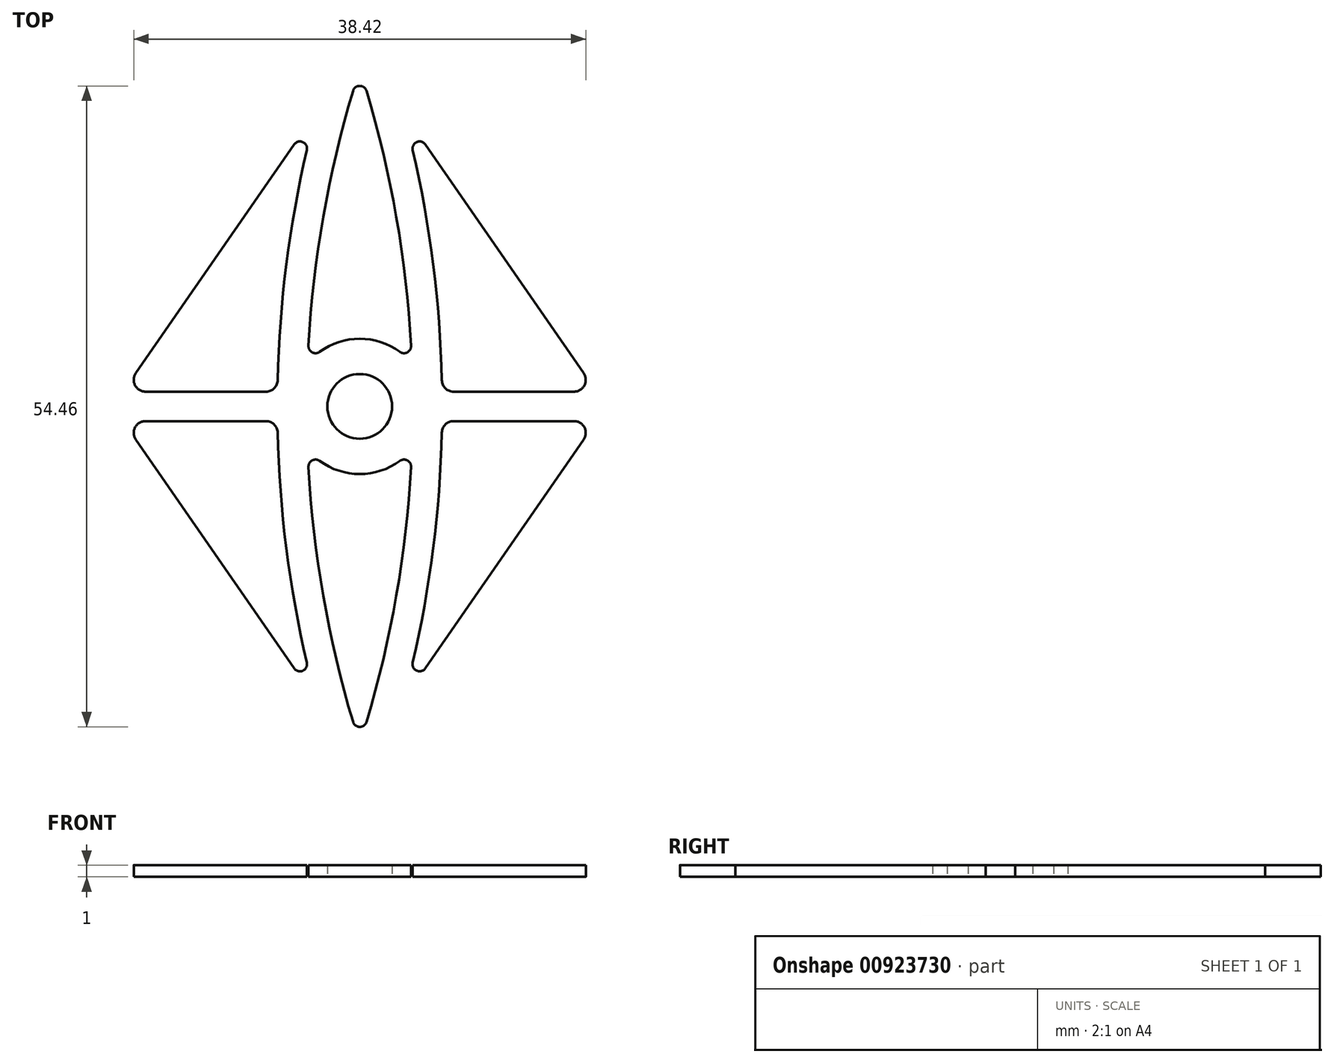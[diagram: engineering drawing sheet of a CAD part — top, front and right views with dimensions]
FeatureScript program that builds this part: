
annotation { "Feature Type Name" : "Feature", "Feature Type Description" : "" }
export const myFeature = defineFeature(function(context is Context, id is Id, definition is map)
    precondition{}
    {
        {
            var Q0;
            Q0=qCreatedBy(makeId("Top.planeOp"),FACE);
            var sketch = newSketch(context, id + "F0", { "sketchPlane" : qUnion([Q0])});
            skLineSegment(sketch, "E0", {"start": v(0, 32.5) * mm, "end": v(0, -32.5) * mm, "construction": true});
            skLineSegment(sketch, "E1", {"start": v(-22.5, 0) * mm, "end": v(22.5, 0) * mm, "construction": true});
            skLineSegment(sketch, "E2", {"start": v(-22.5, 0) * mm, "end": v(0, 32.5) * mm, "construction": true});
            skLineSegment(sketch, "E3", {"start": v(0, 32.5) * mm, "end": v(22.5, 0) * mm, "construction": true});
            skLineSegment(sketch, "E4", {"start": v(22.5, 0) * mm, "end": v(0, -32.5) * mm, "construction": true});
            skLineSegment(sketch, "E5", {"start": v(-22.5, 0) * mm, "end": v(0, -32.5) * mm, "construction": true});
            skLineSegment(sketch, "E6", {"start": v(-22.5, 0) * mm, "end": v(-88.97, 0) * mm, "construction": true});
            skArc(sketch, "E7", {"start": v(0, 32.5) * mm, "mid": v(5.75, 0) * mm, "end": v(0, -32.5) * mm, "construction": true});
            skArc(sketch, "E8.MirrorCS", {"start": v(0, 32.5) * mm, "mid": v(-5.75, 0) * mm, "end": v(0, -32.5) * mm, "construction": true});
            skLineSegment(sketch, "E9.0", {"start": v(-19.03, 2.82) * mm, "end": v(-5.58, 22.25) * mm});
            skLineSegment(sketch, "E10", {"start": v(-18.2, 1.25) * mm, "end": v(-7.97, 1.25) * mm});
            skArc(sketch, "E11.trimOffspring", {"start": v(-4.5, 21.77) * mm, "mid": v(-6.24, 12.06) * mm, "end": v(-6.97, 2.23) * mm});
            skCircle(sketch, "E12", {"center": v(0, 0) * mm, "radius": 5.75 * mm, "construction": true});
            skCircle(sketch, "E13", {"center": v(0, 0) * mm, "radius": 2.75 * mm});
            skArc(sketch, "E14.0", {"start": v(-0.57, 26.8) * mm, "mid": v(-3.1, 16.09) * mm, "end": v(-4.36, 5.15) * mm});
            skArc(sketch, "E14.1", {"start": v(0.57, 26.8) * mm, "mid": v(3.1, 16.09) * mm, "end": v(4.36, 5.15) * mm});
            skArc(sketch, "E15.trimOffspring", {"start": v(3.4, 4.63) * mm, "mid": v(0, 5.75) * mm, "end": v(-3.4, 4.63) * mm});
            skPoint(sketch, "E16.visualSharp", {"position": v(-20.11, 1.25) * mm});
            skArc(sketch, "E16.filletArc", {"start": v(-19.03, 2.82) * mm, "mid": v(-19.1, 1.79) * mm, "end": v(-18.2, 1.25) * mm});
            skPoint(sketch, "E17.visualSharp", {"position": v(-7, 1.25) * mm});
            skArc(sketch, "E17.filletArc", {"start": v(-7.97, 1.25) * mm, "mid": v(-7.28, 1.53) * mm, "end": v(-6.97, 2.23) * mm});
            skPoint(sketch, "E18.visualSharp", {"position": v(-3.7, 24.97) * mm});
            skArc(sketch, "E18.filletArc", {"start": v(-4.5, 21.77) * mm, "mid": v(-4.84, 22.46) * mm, "end": v(-5.58, 22.25) * mm});
            skPoint(sketch, "E19.visualSharp", {"position": v(-4.43, 3.67) * mm});
            skArc(sketch, "E19.filletArc", {"start": v(-4.36, 5.15) * mm, "mid": v(-4.04, 4.6) * mm, "end": v(-3.4, 4.63) * mm});
            skPoint(sketch, "E20.visualSharp", {"position": v(4.43, 3.67) * mm});
            skArc(sketch, "E20.filletArc", {"start": v(3.4, 4.63) * mm, "mid": v(4.04, 4.6) * mm, "end": v(4.36, 5.15) * mm});
            skPoint(sketch, "E21.visualSharp", {"position": v(0, 28.65) * mm});
            skArc(sketch, "E21.filletArc", {"start": v(0.57, 26.8) * mm, "mid": v(0, 27.23) * mm, "end": v(-0.57, 26.8) * mm});
            skArc(sketch, "E22.MirrorCS", {"start": v(4.5, 21.77) * mm, "mid": v(6.24, 12.06) * mm, "end": v(6.97, 2.23) * mm});
            skArc(sketch, "E23.MirrorCS", {"start": v(4.5, 21.77) * mm, "mid": v(4.84, 22.46) * mm, "end": v(5.58, 22.25) * mm});
            skLineSegment(sketch, "E24.MirrorCS", {"start": v(19.03, 2.82) * mm, "end": v(5.58, 22.25) * mm});
            skArc(sketch, "E25.MirrorCS", {"start": v(19.03, 2.82) * mm, "mid": v(19.1, 1.79) * mm, "end": v(18.2, 1.25) * mm});
            skLineSegment(sketch, "E26.MirrorCS", {"start": v(18.2, 1.25) * mm, "end": v(7.97, 1.25) * mm});
            skArc(sketch, "E27.MirrorCS", {"start": v(7.97, 1.25) * mm, "mid": v(7.28, 1.53) * mm, "end": v(6.97, 2.23) * mm});
            skLineSegment(sketch, "E28.MirrorCS", {"start": v(-18.2, -1.25) * mm, "end": v(-7.97, -1.25) * mm});
            skArc(sketch, "E29.MirrorCS", {"start": v(-19.03, -2.82) * mm, "mid": v(-19.1, -1.79) * mm, "end": v(-18.2, -1.25) * mm});
            skLineSegment(sketch, "E30.MirrorCS", {"start": v(-19.03, -2.82) * mm, "end": v(-5.58, -22.25) * mm});
            skArc(sketch, "E31.MirrorCS", {"start": v(-7.97, -1.25) * mm, "mid": v(-7.28, -1.53) * mm, "end": v(-6.97, -2.23) * mm});
            skArc(sketch, "E32.MirrorCS", {"start": v(-4.5, -21.77) * mm, "mid": v(-6.24, -12.06) * mm, "end": v(-6.97, -2.23) * mm});
            skArc(sketch, "E33.MirrorCS", {"start": v(-4.5, -21.77) * mm, "mid": v(-4.84, -22.46) * mm, "end": v(-5.58, -22.25) * mm});
            skArc(sketch, "E34.MirrorCS", {"start": v(-0.57, -26.8) * mm, "mid": v(-3.1, -16.09) * mm, "end": v(-4.36, -5.15) * mm});
            skArc(sketch, "E35.MirrorCS", {"start": v(-4.36, -5.15) * mm, "mid": v(-4.04, -4.6) * mm, "end": v(-3.4, -4.63) * mm});
            skArc(sketch, "E36.MirrorCS", {"start": v(3.4, -4.63) * mm, "mid": v(0, -5.75) * mm, "end": v(-3.4, -4.63) * mm});
            skArc(sketch, "E37.MirrorCS", {"start": v(3.4, -4.63) * mm, "mid": v(4.04, -4.6) * mm, "end": v(4.36, -5.15) * mm});
            skArc(sketch, "E38.MirrorCS", {"start": v(0.57, -26.8) * mm, "mid": v(3.1, -16.09) * mm, "end": v(4.36, -5.15) * mm});
            skArc(sketch, "E39.MirrorCS", {"start": v(0.57, -26.8) * mm, "mid": v(0, -27.23) * mm, "end": v(-0.57, -26.8) * mm});
            skArc(sketch, "E40.MirrorCS", {"start": v(4.5, -21.77) * mm, "mid": v(4.84, -22.46) * mm, "end": v(5.58, -22.25) * mm});
            skArc(sketch, "E41.MirrorCS", {"start": v(4.5, -21.77) * mm, "mid": v(6.24, -12.06) * mm, "end": v(6.97, -2.23) * mm});
            skLineSegment(sketch, "E42.MirrorCS", {"start": v(19.03, -2.82) * mm, "end": v(5.58, -22.25) * mm});
            skArc(sketch, "E43.MirrorCS", {"start": v(19.03, -2.82) * mm, "mid": v(19.1, -1.79) * mm, "end": v(18.2, -1.25) * mm});
            skLineSegment(sketch, "E44.MirrorCS", {"start": v(18.2, -1.25) * mm, "end": v(7.97, -1.25) * mm});
            skArc(sketch, "E45.MirrorCS", {"start": v(7.97, -1.25) * mm, "mid": v(7.28, -1.53) * mm, "end": v(6.97, -2.23) * mm});
            skSolve(sketch);
        }
        {
            var Q0;
            Q0 = qSketchRegion(id + "F0", true);
            extrude(context, id + "F1", {"entities" : qUnion([Q0]), "depth" : 1 * mm, "offsetDistance" : 25 * mm});
        }
    });
